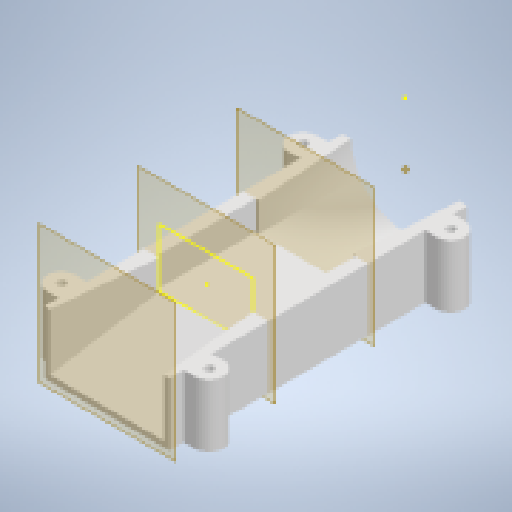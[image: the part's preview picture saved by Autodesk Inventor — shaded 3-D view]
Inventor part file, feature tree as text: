
AUTODESK INVENTOR PART (.ipt)
format: ipt  version: 2025.4 (Build 294407000, 407)  size: 343,552 bytes
history: native  units: mm
features: sketch x13, extrude x7, other x6, loft x2, hole x1
ambient origin geometry x8: Origin, YZ Plane, XZ Plane, XY Plane, X Axis, Y Axis, Z Axis, Center Point
bodies: Body1 (feature_tree)
feature tree (29):
  other  "Bryła1"
  other  "Płaszczyzna konstrukcyjna3"
  other  "Płaszczyzna konstrukcyjna4"
  other  "Płaszczyzna konstrukcyjna5"
  sketch  "Szkic7"
  sketch  "Szkic9"
  sketch  "Szkic10"
  sketch  "Szkic11"
  extrude  "Wyciągnięcie proste1"  Depth=35.0mm
  extrude  "Wyciągnięcie proste2"  Depth=38.0mm
  loft  "Wyciągnięcie złożone1"
  loft  "Wyciągnięcie złożone2"
  extrude  "Wyciągnięcie proste3"  Depth=40.0mm
  sketch  "Szkic14"
  extrude  "Wyciągnięcie proste4"  Depth=40.0mm
  extrude  "Wyciągnięcie proste5"  Depth=44.0mm
  sketch  "Szkic17"
  sketch  "Szkic18"
  extrude  "Wyciągnięcie proste6"  Depth=44.0mm
  hole  "Otwór1"  [1 undecoded]
  extrude  "Wyciągnięcie proste7"  Depth=35.0mm TaperAngle=0.0deg
  sketch  "Szkic12"
  other  "Krawędzie1"
  other  "Krawędzie2"
  sketch  "Szkic13"
  sketch  "Szkic15"
  sketch  "Szkic16"
  sketch  "Szkic19"
  sketch  "Szkic20"
note: 1 required parameter value undecoded (feature->parameter linkage not recoverable at this tier; creation-order binding heuristic only, values carry confidence <= 0.55)
